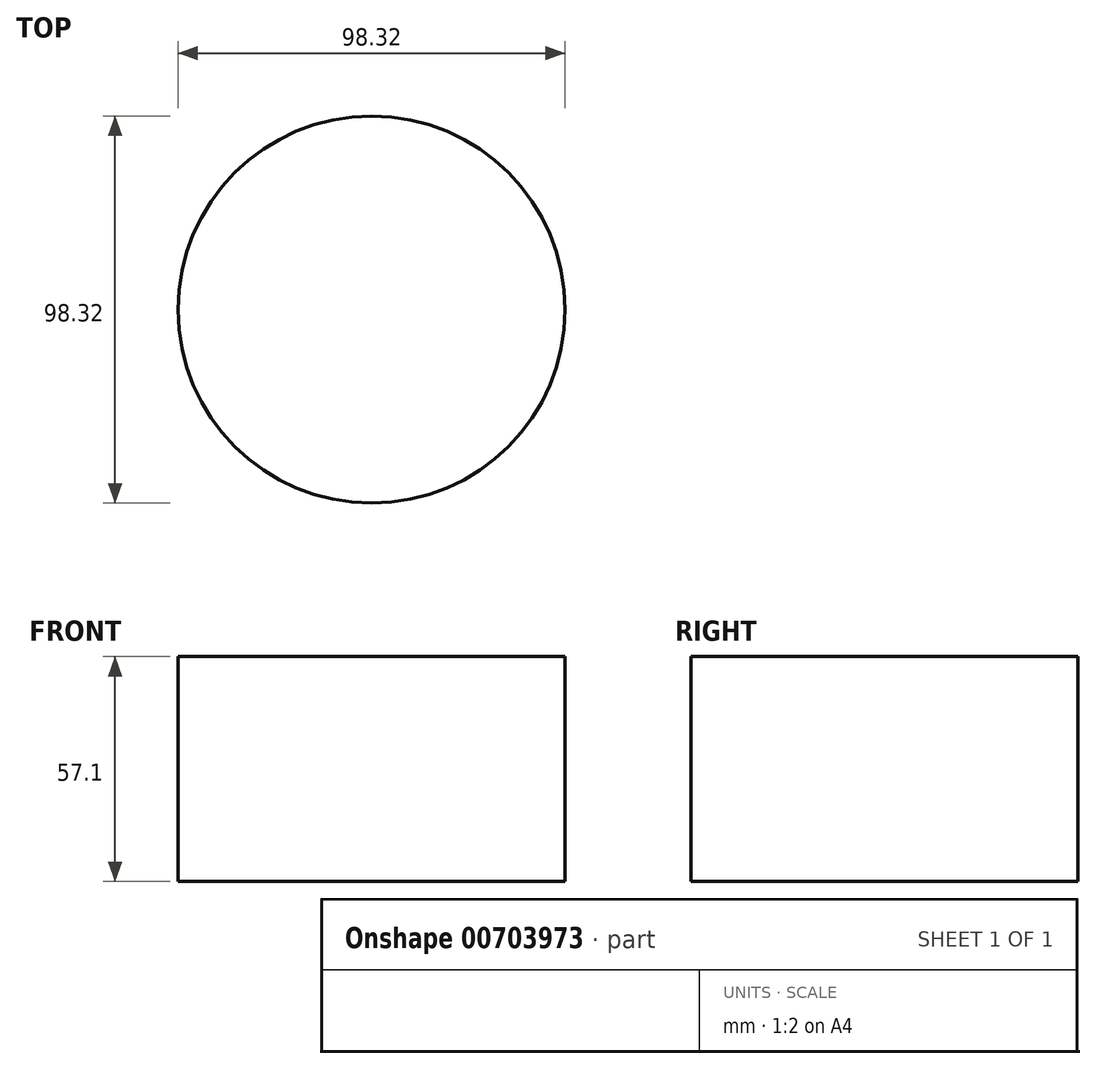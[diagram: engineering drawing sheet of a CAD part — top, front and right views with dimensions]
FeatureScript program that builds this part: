
annotation { "Feature Type Name" : "Feature", "Feature Type Description" : "" }
export const myFeature = defineFeature(function(context is Context, id is Id, definition is map)
    precondition{}
    {
        {
            var Q0;
            Q0=qCreatedBy(makeId("Top.planeOp"),FACE);
            var sketch = newSketch(context, id + "F0", { "sketchPlane" : qUnion([Q0])});
            skCircle(sketch, "E0", {"center": v(0, 0) * mm, "radius": 49.16 * mm});
            skSolve(sketch);
        }
        {
            var Q0;
            Q0=sQuery(id+"F0.wireOp",EDGE,"E0");
            extrude(context, id + "F1", {"bodyType" : ToolBodyType.SURFACE, "surfaceEntities" : qUnion([Q0]), "depth" : 57.1 * mm, "offsetDistance" : 25 * mm});
        }
    });
